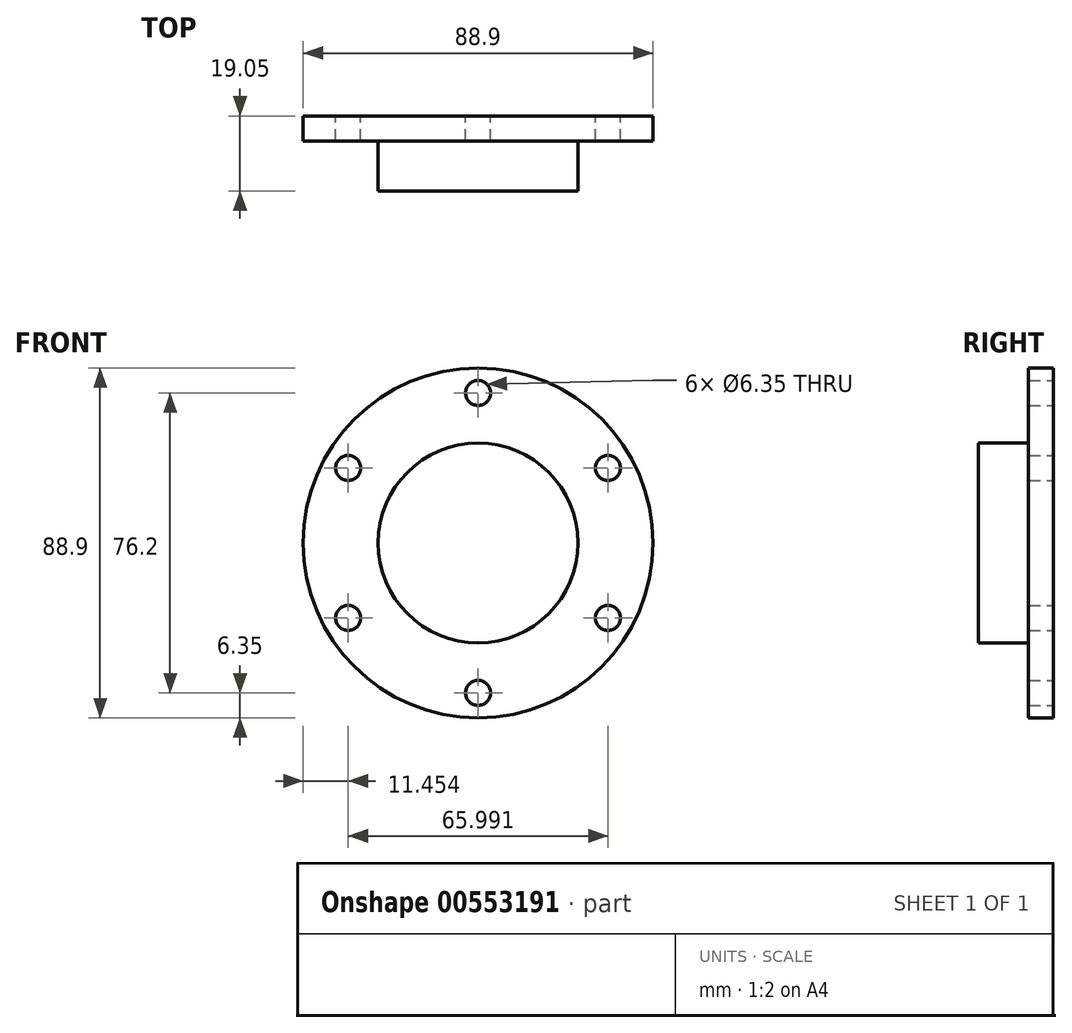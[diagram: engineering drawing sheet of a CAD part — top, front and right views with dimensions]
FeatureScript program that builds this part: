
annotation { "Feature Type Name" : "Feature", "Feature Type Description" : "" }
export const myFeature = defineFeature(function(context is Context, id is Id, definition is map)
    precondition{}
    {
        {
            var Q0;
            Q0=qCreatedBy(makeId("Front.planeOp"),FACE);
            var sketch = newSketch(context, id + "F0", { "sketchPlane" : qUnion([Q0])});
            skCircle(sketch, "E0", {"center": v(0, 0) * mm, "radius": 44.45 * mm});
            skSolve(sketch);
        }
        {
            var Q0;
            Q0=makeQuery(id+"F0.imprint","IMPRINT",FACE,{"disambiguationData":[TD([[makeQuery(id+"F0.imprint","IMPRINT",EDGE,{"derivedFrom":sQuery(id+"F0.wireOp",EDGE,"E0")}),1.0]])]});
            extrude(context, id + "F1", {"entities" : qUnion([Q0]), "depth" : 6.35 * mm, "offsetDistance" : 25.4 * mm});
        }
        {
            var Q0;
            Q0=makeQuery(id+"F1.opExtrude","CAP_FACE",FACE,{"disambiguationData":[OSD([sQuery(id+"F0.wireOp",EDGE,"E0")])],"isStart":false});
            var sketch = newSketch(context, id + "F2", { "sketchPlane" : qUnion([Q0])});
            skCircle(sketch, "E1", {"center": v(0, 0) * mm, "radius": 25.4 * mm});
            skSolve(sketch);
        }
        {
            var Q0;
            Q0=makeQuery(id+"F2.imprint","IMPRINT",FACE,{"disambiguationData":[TD([[makeQuery(id+"F2.imprint","IMPRINT",EDGE,{"derivedFrom":sQuery(id+"F2.wireOp",EDGE,"E1")}),1.0]])]});
            extrude(context, id + "F3", {"entities" : qUnion([Q0]), "operationType" : NewBodyOperationType.ADD, "depth" : 12.7 * mm, "offsetDistance" : 25.4 * mm});
        }
        {
            var Q0;
            Q0=makeQuery(id+"F1.opExtrude","CAP_FACE",FACE,{"disambiguationData":[OSD([sQuery(id+"F0.wireOp",EDGE,"E0")])],"isStart":false});
            cPlane(context, id + "F4", {"entities" : qUnion([Q0]), "cplaneType" : CPlaneType.OFFSET, "offset" : 6.35 * mm, "width" : 152.4 * mm, "height" : 152.4 * mm});
        }
        {
            var Q0;
            Q0=qCreatedBy(id+"F4.planeOp",FACE);
            var sketch = newSketch(context, id + "F5", { "sketchPlane" : qUnion([Q0])});
            skCircle(sketch, "E2", {"center": v(0, 0) * mm, "radius": 28.58 * mm});
            skCircle(sketch, "E3.0", {"center": v(0, 0) * mm, "radius": 25.4 * mm});
            skSolve(sketch);
        }
        {
            var Q0;
            Q0 = qSketchRegion(id + "F5", true);
            extrude(context, id + "F6", {"entities" : qUnion([Q0]), "operationType" : NewBodyOperationType.REMOVE, "depth" : 3.17 * mm, "offsetDistance" : 25.4 * mm, "symmetric" : true});
        }
        {
            var Q0;
            Q0=makeQuery(id+"F1.opExtrude","CAP_FACE",FACE,{"disambiguationData":[OSD([sQuery(id+"F0.wireOp",EDGE,"E0")])],"isStart":true});
            var sketch = newSketch(context, id + "F7", { "sketchPlane" : qUnion([Q0])});
            skLineSegment(sketch, "E4", {"start": v(0, 44.45) * mm, "end": v(0, 38.1) * mm, "construction": true});
            skCircle(sketch, "E5", {"center": v(0, 38.1) * mm, "radius": 3.18 * mm});
            skCircle(sketch, "E6.1.0", {"center": v(-33, 19.05) * mm, "radius": 3.18 * mm});
            skCircle(sketch, "E6.2.0", {"center": v(-33, -19.05) * mm, "radius": 3.18 * mm});
            skCircle(sketch, "E6.3.0", {"center": v(0, -38.1) * mm, "radius": 3.18 * mm});
            skCircle(sketch, "E6.4.0", {"center": v(33, -19.05) * mm, "radius": 3.18 * mm});
            skCircle(sketch, "E6.5.0", {"center": v(33, 19.05) * mm, "radius": 3.18 * mm});
            skPoint(sketch, "E6.center", {"position": v(0, 0) * mm});
            skSolve(sketch);
        }
        {
            var Q0;
            Q0=makeQuery(id+"F7.imprint","IMPRINT",FACE,{"disambiguationData":[TD([[makeQuery(id+"F7.imprint","IMPRINT",EDGE,{"derivedFrom":sQuery(id+"F7.wireOp",EDGE,"E6.1.0")}),1.0]])]});
            var Q1;
            Q1=makeQuery(id+"F7.imprint","IMPRINT",FACE,{"disambiguationData":[TD([[makeQuery(id+"F7.imprint","IMPRINT",EDGE,{"derivedFrom":sQuery(id+"F7.wireOp",EDGE,"E6.2.0")}),1.0]])]});
            var Q2;
            Q2=makeQuery(id+"F7.imprint","IMPRINT",FACE,{"disambiguationData":[TD([[makeQuery(id+"F7.imprint","IMPRINT",EDGE,{"derivedFrom":sQuery(id+"F7.wireOp",EDGE,"E6.3.0")}),1.0]])]});
            var Q3;
            Q3=makeQuery(id+"F7.imprint","IMPRINT",FACE,{"disambiguationData":[TD([[makeQuery(id+"F7.imprint","IMPRINT",EDGE,{"derivedFrom":sQuery(id+"F7.wireOp",EDGE,"E6.4.0")}),1.0]])]});
            var Q4;
            Q4=makeQuery(id+"F7.imprint","IMPRINT",FACE,{"disambiguationData":[TD([[makeQuery(id+"F7.imprint","IMPRINT",EDGE,{"derivedFrom":sQuery(id+"F7.wireOp",EDGE,"E6.5.0")}),1.0]])]});
            var Q5;
            Q5=makeQuery(id+"F7.imprint","IMPRINT",FACE,{"disambiguationData":[TD([[makeQuery(id+"F7.imprint","IMPRINT",EDGE,{"derivedFrom":sQuery(id+"F7.wireOp",EDGE,"E5")}),1.0]])]});
            extrude(context, id + "F8", {"entities" : qUnion([Q0, Q1, Q2, Q3, Q4, Q5]), "operationType" : NewBodyOperationType.REMOVE, "oppositeDirection" : true, "depth" : 25.4 * mm, "offsetDistance" : 25.4 * mm});
        }
    });
